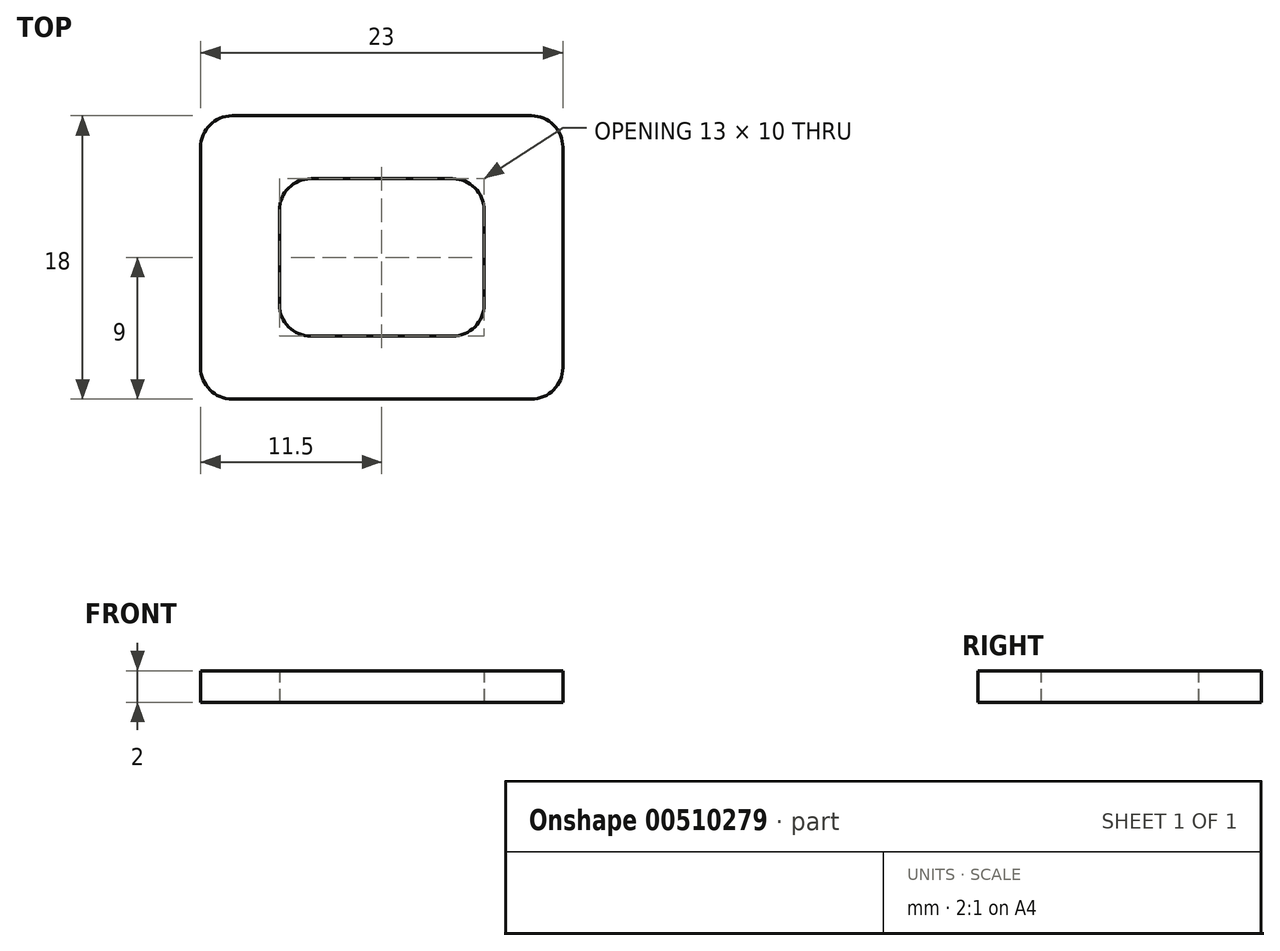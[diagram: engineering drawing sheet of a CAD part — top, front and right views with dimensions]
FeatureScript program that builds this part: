
annotation { "Feature Type Name" : "Feature", "Feature Type Description" : "" }
export const myFeature = defineFeature(function(context is Context, id is Id, definition is map)
    precondition{}
    {
        {
            var Q0;
            Q0=qCreatedBy(makeId("Top.planeOp"),FACE);
            var sketch = newSketch(context, id + "F0", { "sketchPlane" : qUnion([Q0])});
            skLineSegment(sketch, "E0.bottom", {"start": v(2, 0) * mm, "end": v(21, 0) * mm});
            skLineSegment(sketch, "E0.top", {"start": v(2, 18) * mm, "end": v(21, 18) * mm});
            skLineSegment(sketch, "E0.left", {"start": v(0, 2) * mm, "end": v(0, 16) * mm});
            skLineSegment(sketch, "E0.right", {"start": v(23, 2) * mm, "end": v(23, 16) * mm});
            skLineSegment(sketch, "E1", {"start": v(0, 9) * mm, "end": v(23, 9) * mm, "construction": true});
            skLineSegment(sketch, "E2", {"start": v(5, 9) * mm, "end": v(5, 12) * mm});
            skLineSegment(sketch, "E3", {"start": v(7, 14) * mm, "end": v(16, 14) * mm});
            skLineSegment(sketch, "E4", {"start": v(18, 12) * mm, "end": v(18, 9) * mm});
            skLineSegment(sketch, "E5", {"start": v(11.5, 18) * mm, "end": v(11.5, 0) * mm, "construction": true});
            skLineSegment(sketch, "E6.MirrorCS", {"start": v(18, 6) * mm, "end": v(18, 9) * mm});
            skLineSegment(sketch, "E7.MirrorCS", {"start": v(5, 9) * mm, "end": v(5, 6) * mm});
            skLineSegment(sketch, "E8.MirrorCS", {"start": v(7, 4) * mm, "end": v(16, 4) * mm});
            skPoint(sketch, "E9.visualSharp", {"position": v(0, 18) * mm});
            skArc(sketch, "E9.filletArc", {"start": v(2, 18) * mm, "mid": v(0.59, 17.41) * mm, "end": v(0, 16) * mm});
            skPoint(sketch, "E10.visualSharp", {"position": v(23, 18) * mm});
            skArc(sketch, "E10.filletArc", {"start": v(23, 16) * mm, "mid": v(22.41, 17.41) * mm, "end": v(21, 18) * mm});
            skPoint(sketch, "E11.visualSharp", {"position": v(23, 0) * mm});
            skArc(sketch, "E11.filletArc", {"start": v(21, 0) * mm, "mid": v(22.41, 0.59) * mm, "end": v(23, 2) * mm});
            skPoint(sketch, "E12.visualSharp", {"position": v(0, 0) * mm});
            skArc(sketch, "E12.filletArc", {"start": v(0, 2) * mm, "mid": v(0.59, 0.59) * mm, "end": v(2, 0) * mm});
            skPoint(sketch, "E13.visualSharp", {"position": v(5, 4) * mm});
            skArc(sketch, "E13.filletArc", {"start": v(5, 6) * mm, "mid": v(5.59, 4.59) * mm, "end": v(7, 4) * mm});
            skPoint(sketch, "E14.visualSharp", {"position": v(18, 4) * mm});
            skArc(sketch, "E14.filletArc", {"start": v(16, 4) * mm, "mid": v(17.41, 4.59) * mm, "end": v(18, 6) * mm});
            skPoint(sketch, "E15.visualSharp", {"position": v(18, 14) * mm});
            skArc(sketch, "E15.filletArc", {"start": v(18, 12) * mm, "mid": v(17.41, 13.41) * mm, "end": v(16, 14) * mm});
            skPoint(sketch, "E16.visualSharp", {"position": v(5, 14) * mm});
            skArc(sketch, "E16.filletArc", {"start": v(7, 14) * mm, "mid": v(5.59, 13.41) * mm, "end": v(5, 12) * mm});
            skSolve(sketch);
        }
        {
            var Q0;
            Q0=makeQuery(id+"F0.imprint","IMPRINT",FACE,{"disambiguationData":[TD([[makeQuery(id+"F0.imprint","IMPRINT",EDGE,{"derivedFrom":sQuery(id+"F0.wireOp",EDGE,"E0.bottom")}),1.0]])]});
            extrude(context, id + "F1", {"entities" : qUnion([Q0]), "depth" : 2 * mm});
        }
    });
